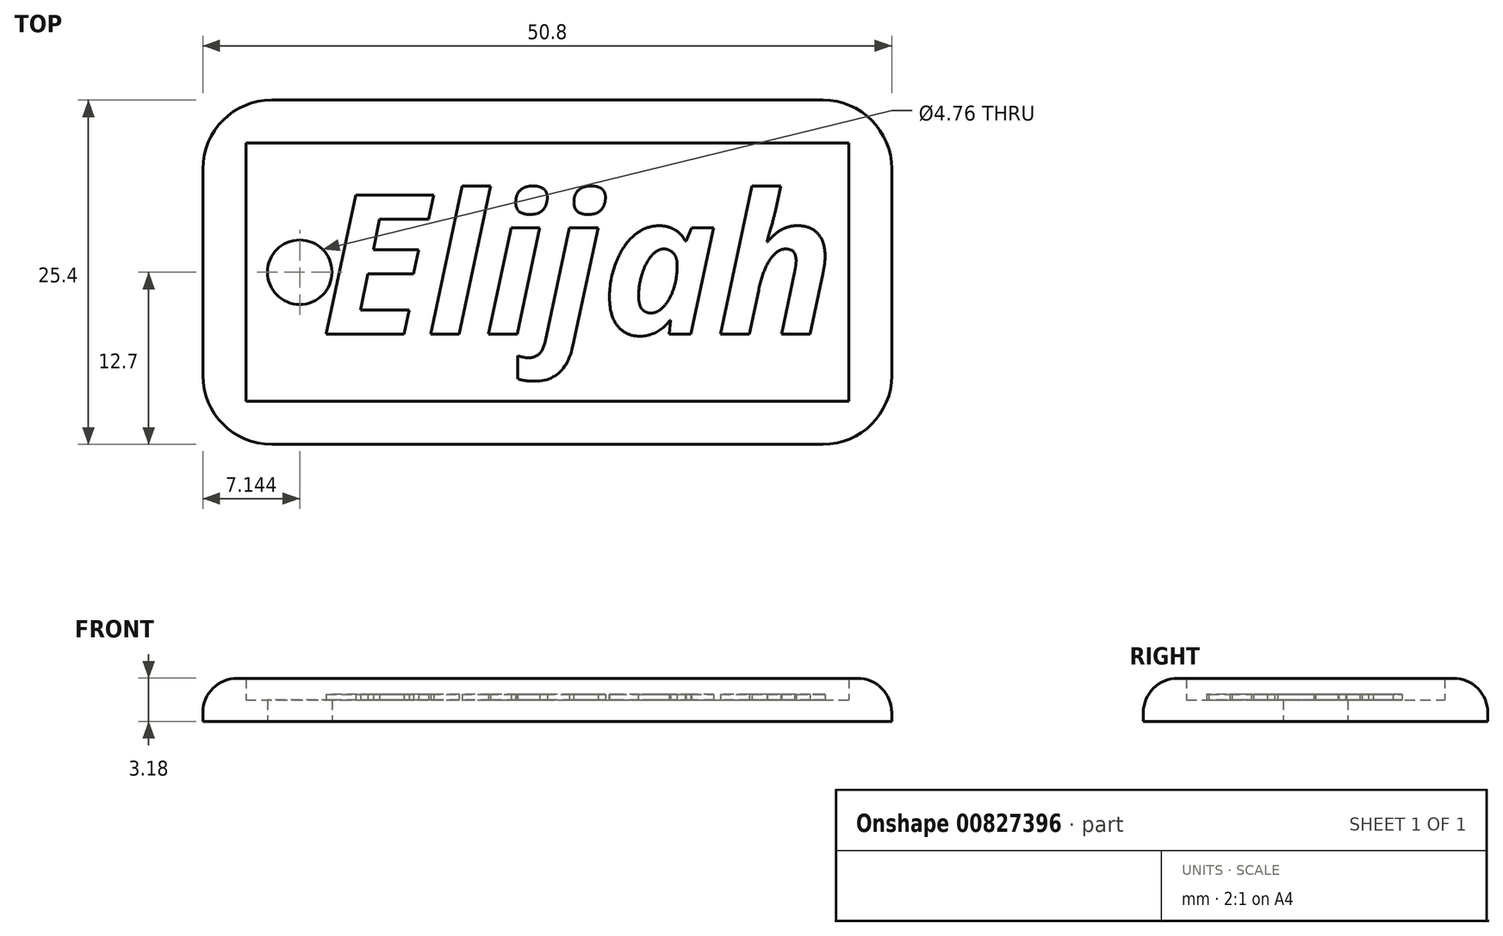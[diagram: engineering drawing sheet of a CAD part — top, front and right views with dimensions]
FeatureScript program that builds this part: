
annotation { "Feature Type Name" : "Feature", "Feature Type Description" : "" }
export const myFeature = defineFeature(function(context is Context, id is Id, definition is map)
    precondition{}
    {
        {
            var Q0;
            Q0=qCreatedBy(makeId("Top.planeOp"),FACE);
            var sketch = newSketch(context, id + "F0", { "sketchPlane" : qUnion([Q0])});
            skLineSegment(sketch, "E0.bottom", {"start": v(0, 0) * mm, "end": v(50.8, 0) * mm});
            skLineSegment(sketch, "E0.top", {"start": v(0, 25.4) * mm, "end": v(50.8, 25.4) * mm});
            skLineSegment(sketch, "E0.left", {"start": v(0, 0) * mm, "end": v(0, 25.4) * mm});
            skLineSegment(sketch, "E0.right", {"start": v(50.8, 0) * mm, "end": v(50.8, 25.4) * mm});
            skCircle(sketch, "E1", {"center": v(7.14, 12.7) * mm, "radius": 2.38 * mm});
            skPoint(sketch, "E1.centerSnap0", {"position": v(0, 12.7) * mm});
            skLineSegment(sketch, "E2.0", {"start": v(3.18, 22.23) * mm, "end": v(47.62, 22.23) * mm});
            skLineSegment(sketch, "E2.1", {"start": v(3.18, 3.18) * mm, "end": v(3.18, 22.22) * mm});
            skLineSegment(sketch, "E2.2", {"start": v(3.18, 3.18) * mm, "end": v(47.62, 3.18) * mm});
            skLineSegment(sketch, "E2.3", {"start": v(47.62, 3.18) * mm, "end": v(47.62, 22.23) * mm});
            skSolve(sketch);
        }
        {
            var Q0;
            Q0=makeQuery(id+"F0.imprint","IMPRINT",FACE,{"disambiguationData":[TD([[makeQuery(id+"F0.imprint","IMPRINT",EDGE,{"derivedFrom":sQuery(id+"F0.wireOp",EDGE,"E1")}),-1.0]])]});
            extrude(context, id + "F1", {"entities" : qUnion([Q0]), "depth" : 1.59 * mm, "offsetDistance" : 25.4 * mm});
        }
        {
            var Q0;
            Q0 = qSketchRegion(id + "F0", true);
            extrude(context, id + "F2", {"entities" : qUnion([Q0]), "operationType" : NewBodyOperationType.ADD, "depth" : 3.17 * mm, "offsetDistance" : 25.4 * mm});
        }
        {
            var Q0;
            Q0=makeQuery(id+"F2.opExtrude","SWEPT_EDGE",EDGE,{"disambiguationData":[OSD([sQuery(id+"F0.wireOp",EDGE,"E0.bottom"),sQuery(id+"F0.wireOp",EDGE,"E0.right")])]});
            var Q1;
            Q1=makeQuery(id+"F2.opExtrude","SWEPT_EDGE",EDGE,{"disambiguationData":[OSD([sQuery(id+"F0.wireOp",EDGE,"E0.top"),sQuery(id+"F0.wireOp",EDGE,"E0.right")])]});
            var Q2;
            Q2=makeQuery(id+"F2.opExtrude","SWEPT_EDGE",EDGE,{"disambiguationData":[OSD([sQuery(id+"F0.wireOp",EDGE,"E0.bottom"),sQuery(id+"F0.wireOp",EDGE,"E0.left")])]});
            var Q3;
            Q3=makeQuery(id+"F2.opExtrude","SWEPT_EDGE",EDGE,{"disambiguationData":[OSD([sQuery(id+"F0.wireOp",EDGE,"E0.top"),sQuery(id+"F0.wireOp",EDGE,"E0.left")])]});
            fillet(context, id + "F3", {"entities" : qUnion([Q0, Q1, Q2, Q3]), "radius" : 5.08 * mm, "tangentPropagation" : true, "allowEdgeOverflow" : false});
        }
        {
            var Q0;
            Q0=makeQuery(id+"F2.opExtrude","CAP_EDGE",EDGE,{"disambiguationData":[OSD([sQuery(id+"F0.wireOp",EDGE,"E0.top")])],"isStart":false});
            fillet(context, id + "F4", {"entities" : qUnion([Q0]), "radius" : 2.54 * mm, "tangentPropagation" : true, "allowEdgeOverflow" : false});
        }
        {
            var Q0;
            Q0=makeQuery(id+"F1.opExtrude","CAP_FACE",FACE,{"disambiguationData":[OSD([sQuery(id+"F0.wireOp",EDGE,"E1"),sQuery(id+"F0.wireOp",EDGE,"E2.0"),sQuery(id+"F0.wireOp",EDGE,"E2.1"),sQuery(id+"F0.wireOp",EDGE,"E2.2"),sQuery(id+"F0.wireOp",EDGE,"E2.3")])],"isStart":false});
            var sketch = newSketch(context, id + "F5", { "sketchPlane" : qUnion([Q0])});
            skText(sketch, "E3", { "text": "Elijah ", "fontName": "OpenSans-BoldItalic.ttf"});
            const initialGuessF5  = {"E3": [0.00872, 0.00812, 1, 0, 0.01037]};
            skSetInitialGuess(sketch, initialGuessF5);
            skSolve(sketch);
        }
        {
            var Q0;
            Q0 = qSketchRegion(id + "F5", true);
            extrude(context, id + "F6", {"entities" : qUnion([Q0]), "operationType" : NewBodyOperationType.ADD, "depth" : 0.4 * mm, "offsetDistance" : 25.4 * mm});
        }
    });
